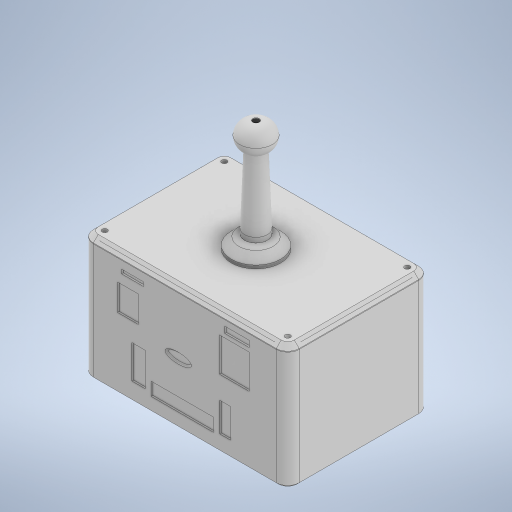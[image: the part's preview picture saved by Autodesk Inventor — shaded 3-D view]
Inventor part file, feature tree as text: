
AUTODESK INVENTOR PART (.ipt)
format: ipt  version: 2023 (Build 270158030, 158C)  size: 1,014,784 bytes
history: native  units: mm
features: sketch x23, extrude x21, projected_geometry x16, chamfer x7, other x5, fillet x4, mirror x3, plane x1, loft x1, pattern_circular x1, revolve x1
ambient origin geometry x8: Origin, YZ Plane, XZ Plane, XY Plane, X Axis, Y Axis, Z Axis, Center Point
bodies: Body1 (feature_tree), Body2 (feature_tree), Body3 (feature_tree), Body4 (feature_tree)
feature tree (83):
  other  "base-plate"
  extrude  "Extrusion1"  Depth=83.0mm
  extrude  "Extrusion2"  Depth=3.5mm
  fillet  "Fillet1"  Radius=3.5mm
  extrude  "Extrusion3"  Depth=5.0mm
  extrude  "Extrusion4"  Depth=5.0mm
  extrude  "Extrusion6"  TaperAngle=0.0deg  [1 undecoded]
  extrude  "Extrusion7"  Depth=10.0mm
  chamfer  "Chamfer1"  Distance=2.0mm
  extrude  "Extrusion8"  Depth=1.5mm TaperAngle=0.0deg
  chamfer  "Chamfer2"  Distance=1.0mm
  chamfer  "Chamfer3"  Distance=5.0mm
  extrude  "Extrusion9"  Depth=2.0mm
  plane  "Work Plane1"
  sketch  "Sketch11"  dims[d23=8.0mm]
  loft  "Loft1"
  chamfer  "Chamfer4"  Distance=1.5mm Angle=45.0deg
  pattern_circular  "Circular Pattern1"  Count=2 Angle=360.0deg
  mirror  "Mirror1"
  chamfer  "Chamfer5"  Distance=2.0mm Angle=45.0deg
  extrude  "Extrusion10"  Depth=1.5mm TaperAngle=0.0deg
  extrude  "Extrusion11"  Depth=8.0mm
  chamfer  "Chamfer6"  Distance=8.0mm
  extrude  "Extrusion12"  Depth=5.0mm
  chamfer  "Chamfer7"  Distance=10.0mm
  fillet  "Fillet2"  [1 undecoded]
  extrude  "Extrusion13"  Depth=2.0mm
  extrude  "Extrusion14"  Depth=10.0mm TaperAngle=0.0deg
  extrude  "Extrusion15"  Depth=3.0mm TaperAngle=0.0deg
  extrude  "Extrusion16"  Depth=24.0mm
  extrude  "Extrusion17"  TaperAngle=0.0deg  [1 undecoded]
  extrude  "Extrusion18"  Depth=24.0mm
  fillet  "Fillet3"  Radius=15.0mm
  revolve  "Revolution1"  [1 undecoded]
  extrude  "Extrusion19"  Depth=0.4mm
  extrude  "Extrusion20"  Depth=0.4mm
  sketch  "Sketch26"  dims[d67=3.0mm d68=2.0mm d69=45.0deg d70=30.0mm d71=8.0mm d72=0.0mm]
  extrude  "Extrusion21"  Depth=0.4mm
  fillet  "Fillet4"  [1 undecoded]
  mirror  "Mirror2"
  mirror  "Mirror3"
  extrude  "Extrusion22"  TaperAngle=0.0deg  [1 undecoded]
  sketch  "Sketch1"  dims[d0=121.75mm d1=83.0mm]
  sketch  "Sketch2"  dims[d2=60.875mm d3=41.5mm d4=3.5mm d5=0.0mm]
  sketch  "Sketch3"  dims[d6=3.2mm d7=5.0mm]
  projected_geometry  "Projected Loop1"
  other  "head"
  sketch  "Sketch4"  dims[d8=5.0mm d9=5.0mm]
  projected_geometry  "Projected Loop2"
  sketch  "Sketch5"  dims[d10=5.0mm d11=0.0mm d12=0.0mm]
  sketch  "Sketch6"  dims[d13=5.0mm d14=10.0mm]
  sketch  "Sketch7"  dims[d15=2.0mm d16=2.0mm d17=0.0mm]
  projected_geometry  "Projected Loop3"
  projected_geometry  "Projected Loop4"
  projected_geometry  "Projected Loop5"
  projected_geometry  "Projected Loop6"
  sketch  "Sketch9"  dims[d18=1.5mm d19=70.0mm d20=0.0mm]
  projected_geometry  "Projected Loop7"
  projected_geometry  "Projected Loop8"
  projected_geometry  "Projected Loop9"
  projected_geometry  "Projected Loop10"
  sketch  "Sketch13"  dims[d24=46.0mm d26=1.0mm d27=0.0mm]
  projected_geometry  "Projected Loop11"
  other  "lid"
  sketch  "Sketch14"  dims[d28=10.0mm]
  projected_geometry  "Projected Loop12"
  sketch  "Sketch15"  dims[d29=77.5mm]
  sketch  "Sketch16"  dims[d30=10.0mm d31=5.0mm d32=0.0mm]
  sketch  "Sketch17"  dims[d33=5.0mm d34=2.0mm d35=45.0deg d36=2.9mm]
  projected_geometry  "Projected Loop13"
  other  "antenna"
  sketch  "Sketch18"  dims[d37=8.0mm d38=0.0mm d39=1.0mm d40=2.0mm d41=45.0deg d42=1.5mm d43=2.0mm d44=45.0deg]
  sketch  "Sketch19"  dims[d45=12.0mm]
  projected_geometry  "Projected Loop14"
  sketch  "Sketch20"  dims[d46=6.0mm d47=0.0mm]
  sketch  "Sketch21"  dims[d48=15.0mm]
  sketch  "Sketch23"  dims[d49=3.0mm]
  sketch  "Sketch24"  dims[d50=0.0mm d51=90.0deg d52=0.0mm d53=90.0deg d54=1.49mm d55=2.0mm d56=45.0deg d57=20.0mm d58=360.0deg d60=1.49mm d61=2.0mm d62=45.0deg]
  projected_geometry  "Projected Loop15"
  sketch  "Sketch25"  dims[d63=2.0mm d64=0.0mm d65=1.5mm d66=0.0mm]
  other  "Edges1"
  sketch  "Sketch27"  dims[d73=6.0mm d74=2.0mm d75=45.0deg d76=5.0mm d77=10.0mm d78=0.0mm d79=0.0mm d80=2.0mm d81=10.0mm d82=0.0mm d83=3.0mm d84=0.0mm d85=42.0mm d86=-0.349066mm d87=0.0mm d88=0.0mm d89=20.0mm d90=15.0mm d91=0.0mm d92=8.0mm d93=0.4mm d94=0.4mm d95=0.4mm d96=90.0deg d97=0.0mm d98=0.0mm d99=3.0mm d100=6.0mm d101=12.0mm d102=26.5mm d103=33.5mm d104=20.0mm d105=4.5mm d106=40.0mm d107=28.5mm d108=9.5mm d109=36.0mm d110=27.0mm d111=41.0mm d112=29.5mm d113=0.0mm d114=0.0mm d115=18.0mm d116=6.3mm d117=13.25mm d118=7.2mm d119=10.0mm d120=0.0mm d121=2.0mm d122=3.0mm d123=3.0mm d124=24.0mm d125=24.0mm d126=0.0mm d127=0.0mm]
  projected_geometry  "Projected Loop16"
note: 6 required parameter values undecoded (feature->parameter linkage not recoverable at this tier; creation-order binding heuristic only, values carry confidence <= 0.55)